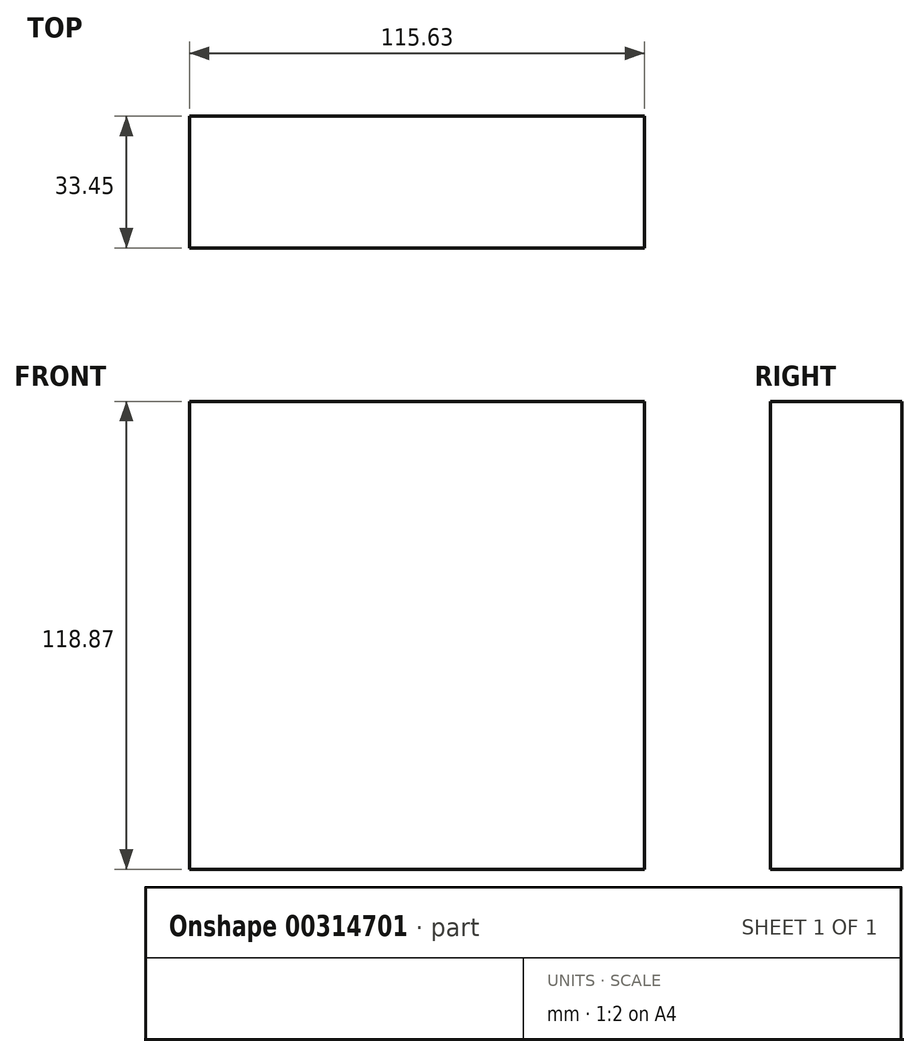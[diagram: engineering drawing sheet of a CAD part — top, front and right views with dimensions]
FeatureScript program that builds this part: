
annotation { "Feature Type Name" : "Feature", "Feature Type Description" : "" }
export const myFeature = defineFeature(function(context is Context, id is Id, definition is map)
    precondition{}
    {
        {
            var Q0;
            Q0=qCreatedBy(makeId("Front.planeOp"),FACE);
            var sketch = newSketch(context, id + "F0", { "sketchPlane" : qUnion([Q0])});
            skLineSegment(sketch, "E0.bottom", {"start": v(-53.16, 64.58) * mm, "end": v(62.47, 64.58) * mm});
            skLineSegment(sketch, "E0.top", {"start": v(-53.16, -54.29) * mm, "end": v(62.47, -54.29) * mm});
            skLineSegment(sketch, "E0.left", {"start": v(-53.16, 64.58) * mm, "end": v(-53.16, -54.29) * mm});
            skLineSegment(sketch, "E0.right", {"start": v(62.47, 64.58) * mm, "end": v(62.47, -54.29) * mm});
            skSolve(sketch);
        }
        {
            var Q0;
            Q0=makeQuery(id+"F0.imprint","IMPRINT",FACE,{"disambiguationData":[TD([[makeQuery(id+"F0.imprint","IMPRINT",EDGE,{"derivedFrom":sQuery(id+"F0.wireOp",EDGE,"E0.bottom")}),-1.0]])]});
            extrude(context, id + "F1", {"entities" : qUnion([Q0]), "oppositeDirection" : true, "depth" : 33.45 * mm});
        }
    });
